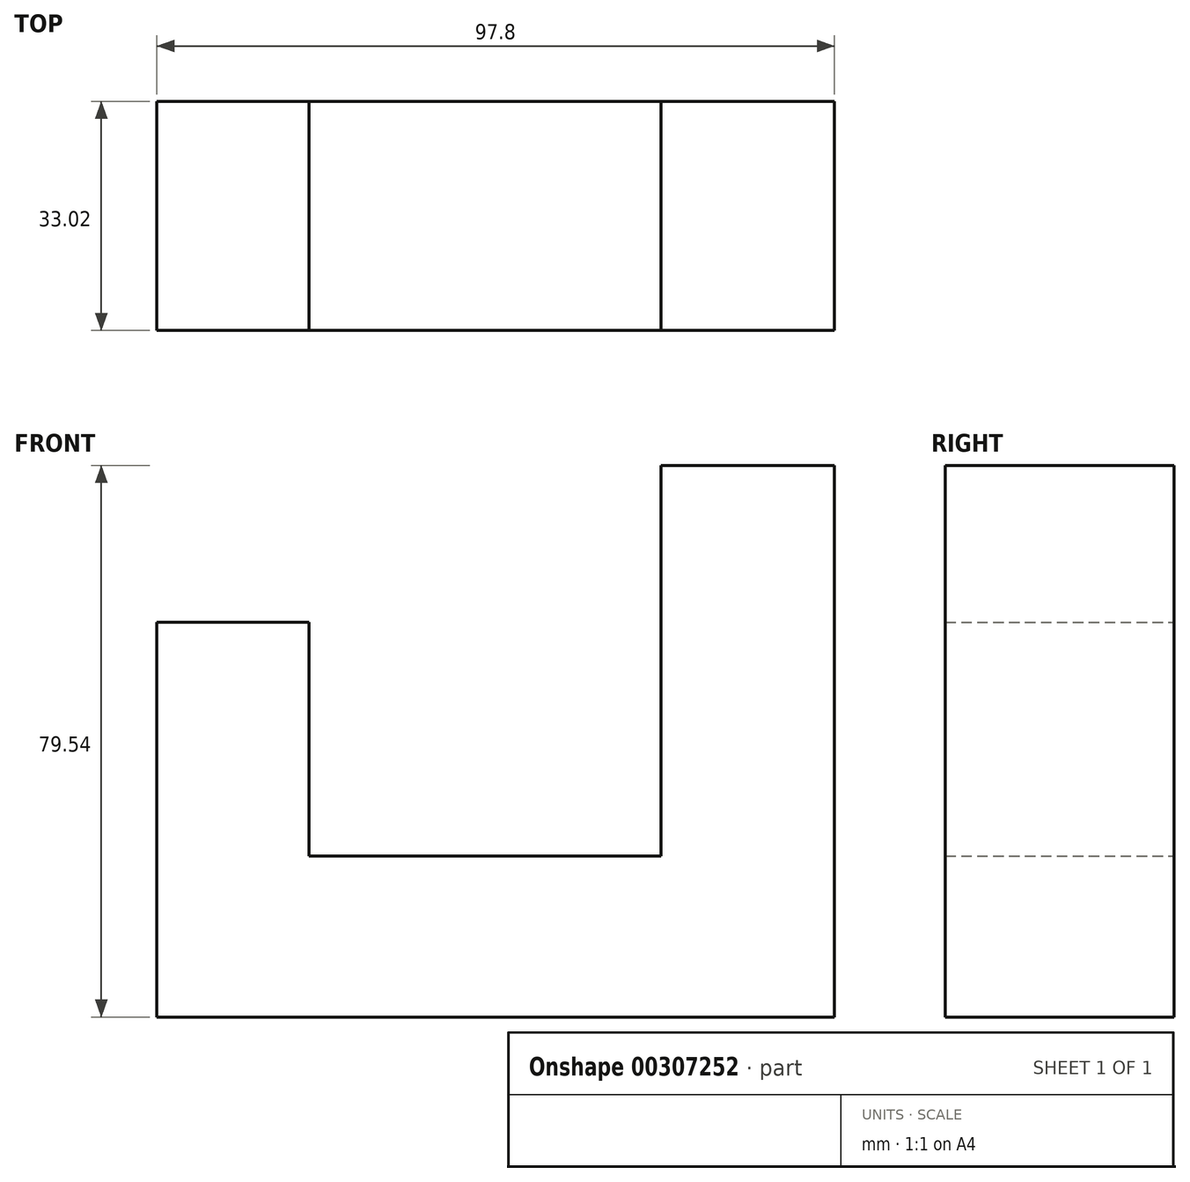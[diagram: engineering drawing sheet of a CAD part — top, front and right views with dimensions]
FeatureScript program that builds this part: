
annotation { "Feature Type Name" : "Feature", "Feature Type Description" : "" }
export const myFeature = defineFeature(function(context is Context, id is Id, definition is map)
    precondition{}
    {
        {
            var Q0;
            Q0=qCreatedBy(makeId("Front.planeOp"),FACE);
            var sketch = newSketch(context, id + "F0", { "sketchPlane" : qUnion([Q0])});
            skLineSegment(sketch, "E0", {"start": v(-42.4, -45.96) * mm, "end": v(55.4, -45.96) * mm});
            skLineSegment(sketch, "E1", {"start": v(55.4, -45.96) * mm, "end": v(55.4, 33.58) * mm});
            skLineSegment(sketch, "E2", {"start": v(55.4, 33.58) * mm, "end": v(30.33, 33.58) * mm});
            skLineSegment(sketch, "E3", {"start": v(30.33, 33.58) * mm, "end": v(30.33, -22.75) * mm});
            skLineSegment(sketch, "E4", {"start": v(30.33, -22.75) * mm, "end": v(-20.43, -22.75) * mm});
            skLineSegment(sketch, "E5", {"start": v(-20.43, -22.75) * mm, "end": v(-20.43, 10.98) * mm});
            skLineSegment(sketch, "E6", {"start": v(-20.43, 10.98) * mm, "end": v(-42.4, 10.98) * mm});
            skLineSegment(sketch, "E7", {"start": v(-42.4, 10.98) * mm, "end": v(-42.4, -45.96) * mm});
            skSolve(sketch);
        }
        {
            var Q0;
            Q0=makeQuery(id+"F0.imprint","IMPRINT",FACE,{"disambiguationData":[TD([[makeQuery(id+"F0.imprint","IMPRINT",EDGE,{"derivedFrom":sQuery(id+"F0.wireOp",EDGE,"E0")}),1.0]])]});
            extrude(context, id + "F1", {"entities" : qUnion([Q0]), "depth" : 33.02 * mm});
        }
    });
